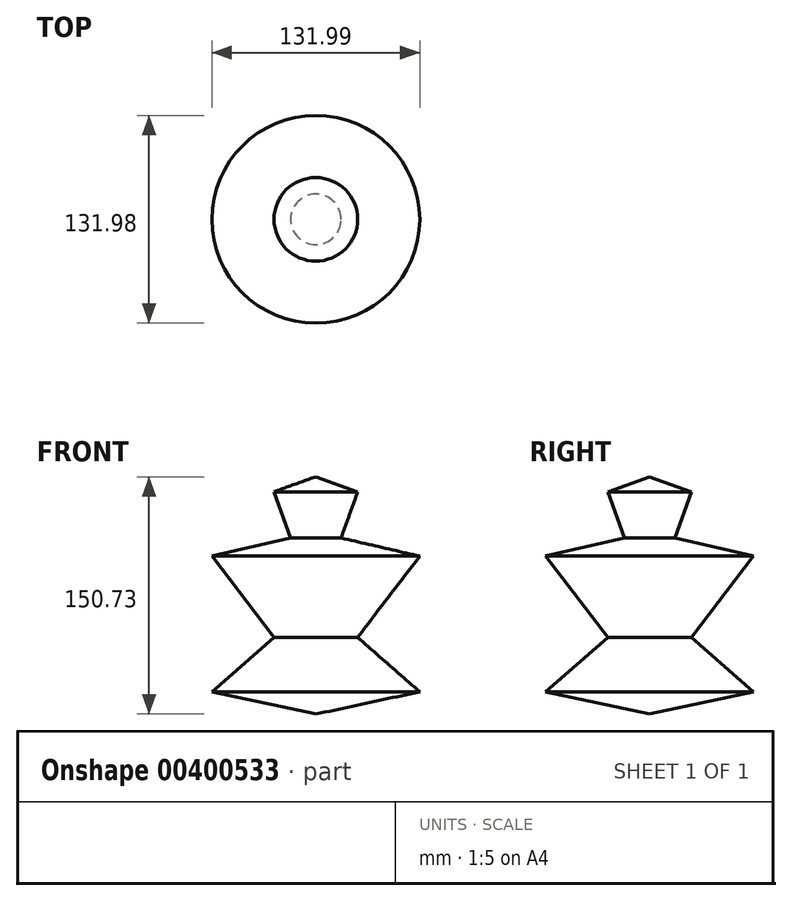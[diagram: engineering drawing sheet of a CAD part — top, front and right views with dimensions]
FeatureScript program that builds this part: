
annotation { "Feature Type Name" : "Feature", "Feature Type Description" : "" }
export const myFeature = defineFeature(function(context is Context, id is Id, definition is map)
    precondition{}
    {
        {
            var Q0;
            Q0=qCreatedBy(makeId("Front.planeOp"),FACE);
            var sketch = newSketch(context, id + "F0", { "sketchPlane" : qUnion([Q0])});
            skLineSegment(sketch, "E0", {"start": v(-31.82, 75.35) * mm, "end": v(-31.82, -75.38) * mm});
            skLineSegment(sketch, "E1", {"start": v(-31.82, 75.35) * mm, "end": v(-5.27, 65.84) * mm});
            skLineSegment(sketch, "E2", {"start": v(-5.27, 65.84) * mm, "end": v(-15.8, 36.46) * mm});
            skLineSegment(sketch, "E3", {"start": v(-15.8, 36.46) * mm, "end": v(34.17, 24.9) * mm});
            skLineSegment(sketch, "E4", {"start": v(34.17, 24.9) * mm, "end": v(-5.27, -26.66) * mm});
            skLineSegment(sketch, "E5", {"start": v(-5.27, -26.66) * mm, "end": v(34.17, -61.29) * mm});
            skLineSegment(sketch, "E6", {"start": v(34.17, -61.29) * mm, "end": v(-31.82, -75.38) * mm});
            skSolve(sketch);
        }
        {
            var Q0;
            Q0=makeQuery(id+"F0.imprint","IMPRINT",FACE,{"disambiguationData":[TD([[makeQuery(id+"F0.imprint","IMPRINT",EDGE,{"derivedFrom":sQuery(id+"F0.wireOp",EDGE,"E0")}),1.0]])]});
            var Q1;
            Q1=sQuery(id+"F0.wireOp",EDGE,"E0");
            revolve(context, id + "F1", {"entities" : qUnion([Q0]), "axis" : qUnion([Q1]), "revolveType" : RevolveType.FULL});
        }
    });
